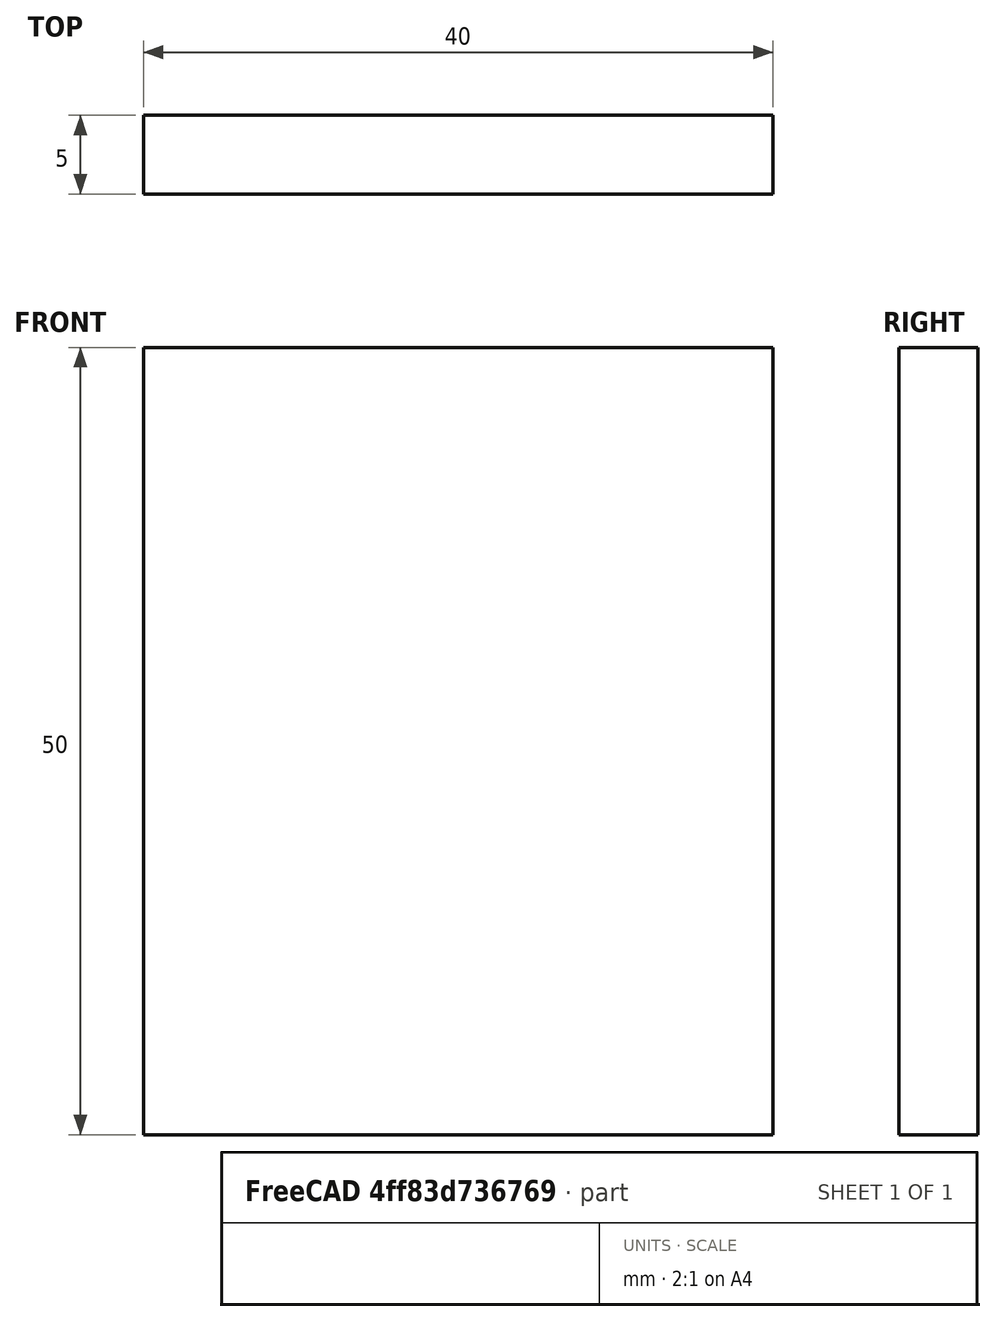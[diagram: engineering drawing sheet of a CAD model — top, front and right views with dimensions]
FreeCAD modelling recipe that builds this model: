
FCSTD DOCUMENT  (FreeCAD 0.15R4671 (Git))
Label: Flat Bar 40x5 EN10058 S235JR
License: All rights reserved
LicenseURL: http://en.wikipedia.org/wiki/All_rights_reserved
objects: Sketcher::SketchObject×1, Part::Extrusion×1
note: 2 computed .brp shape members not serialized (recipe doc carries the construction recipe); baked Part::Feature solids carry a one-line shape summary decoded from their .brp

FEATURE [Sketcher::SketchObject] Sketch
  sketch-geometry (4):
    g0: LineSegment StartX=-20 StartY=-2.5 StartZ=0 EndX=20 EndY=-2.5 EndZ=0
    g1: LineSegment StartX=20 StartY=-2.5 StartZ=0 EndX=20 EndY=2.5 EndZ=0
    g2: LineSegment StartX=20 StartY=2.5 StartZ=0 EndX=-20 EndY=2.5 EndZ=0
    g3: LineSegment StartX=-20 StartY=2.5 StartZ=0 EndX=-20 EndY=-2.5 EndZ=0
  constraints (12):
    c: Coincident(g0,g1)
    c: Coincident(g1,g2)
    c: Coincident(g2,g3)
    c: Coincident(g3,g0)
    c: Horizontal(g0)
    c: Horizontal(g2)
    c: Vertical(g1)
    c: Vertical(g3)
    c: Symmetric(g1,g2,g-2)
    c: Symmetric(g0,g1,g-1)
    c: DistanceY(g1) = 5
    c: DistanceX(g0) = 40
FEATURE [Part::Extrusion] Extrude  label="Flat Bar 40x5 EN10058 S235JR"
  Base = -> Sketch
  Dir = (0,0,50)
  Solid = true
